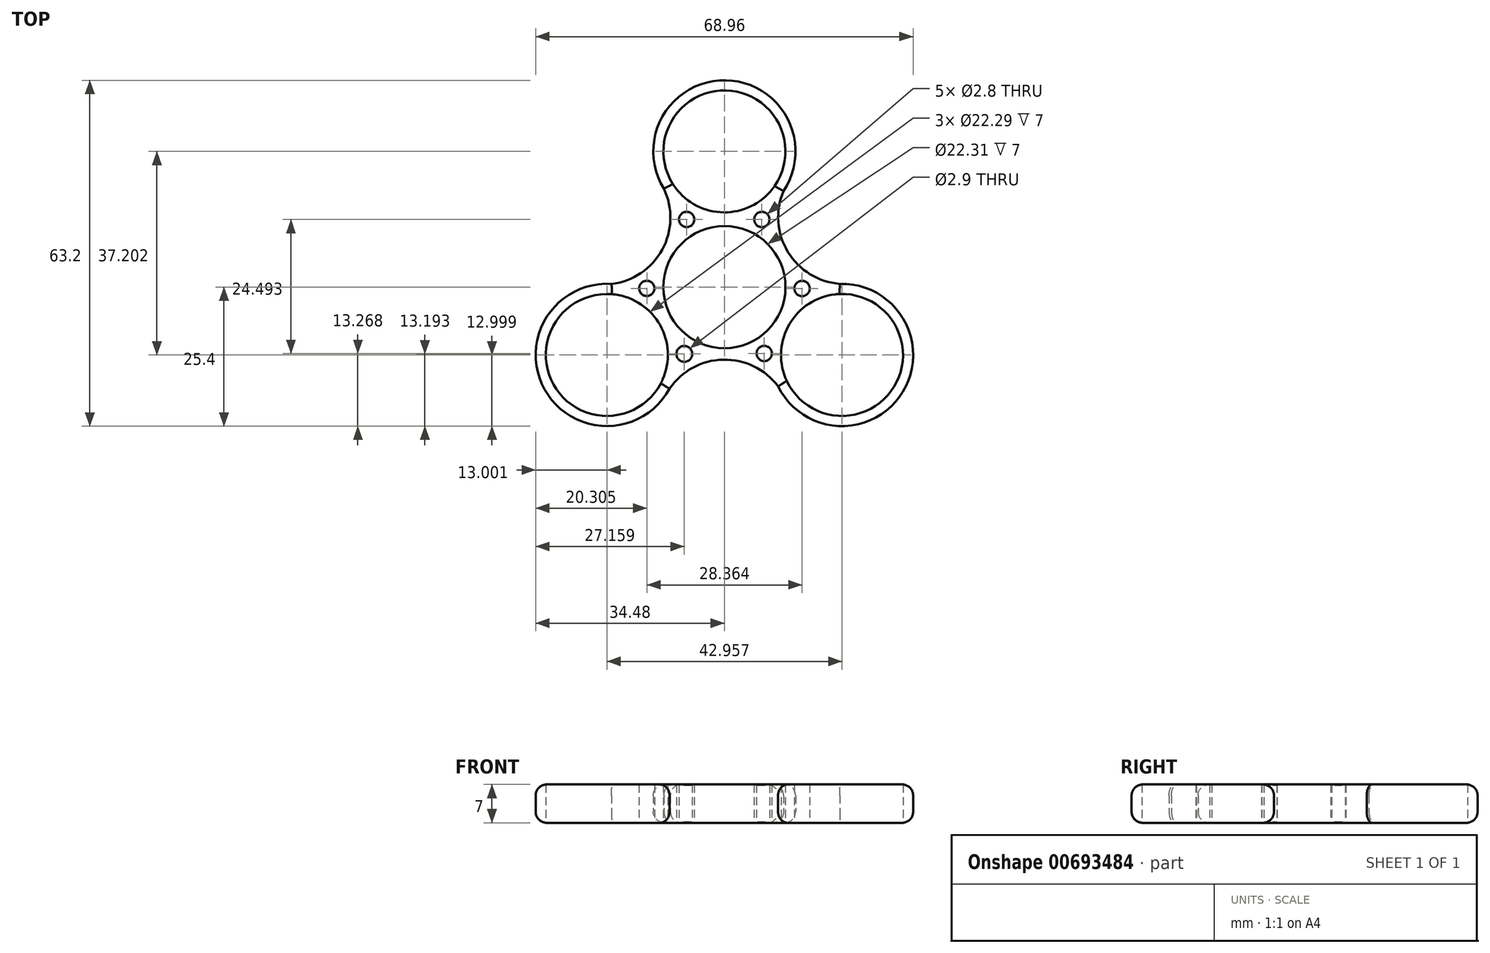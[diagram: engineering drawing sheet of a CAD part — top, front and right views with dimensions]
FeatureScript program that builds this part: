
annotation { "Feature Type Name" : "Feature", "Feature Type Description" : "" }
export const myFeature = defineFeature(function(context is Context, id is Id, definition is map)
    precondition{}
    {
        {
            var Q0;
            Q0=qCreatedBy(makeId("Top.planeOp"),FACE);
            var sketch = newSketch(context, id + "F0", { "sketchPlane" : qUnion([Q0])});
            skCircle(sketch, "E0", {"center": v(0, 0) * mm, "radius": 11.15 * mm});
            skCircle(sketch, "E1", {"center": v(0, 0) * mm, "radius": 13 * mm});
            skCircle(sketch, "E2", {"center": v(0, 24.8) * mm, "radius": 11.14 * mm});
            skCircle(sketch, "E3", {"center": v(0, 24.8) * mm, "radius": 13 * mm});
            skCircle(sketch, "E4.1.0", {"center": v(-21.48, -12.4) * mm, "radius": 13 * mm});
            skCircle(sketch, "E4.1.1", {"center": v(-21.48, -12.4) * mm, "radius": 11.14 * mm});
            skCircle(sketch, "E4.2.0", {"center": v(21.48, -12.4) * mm, "radius": 13 * mm});
            skCircle(sketch, "E4.2.1", {"center": v(21.48, -12.4) * mm, "radius": 11.14 * mm});
            skArc(sketch, "E5", {"start": v(-20.6, 0.57) * mm, "mid": v(-11.37, 6.82) * mm, "end": v(-11.06, 17.97) * mm});
            skArc(sketch, "E6.1.0", {"start": v(9.8, -18.12) * mm, "mid": v(-0.22, -13.26) * mm, "end": v(-10.03, -18.56) * mm});
            skArc(sketch, "E6.2.0", {"start": v(10.8, 17.56) * mm, "mid": v(11.6, 6.44) * mm, "end": v(21.09, 0.6) * mm});
            skSolve(sketch);
        }
        {
            var Q0;
            {var subQ0=sQuery(id+"F0.wireOp",EDGE,"E3");var subQ1=sQuery(id+"F0.wireOp",EDGE,"E1");var subQ2=makeQuery(id+"F0.imprint","INTERSECT",VERTEX,{"disambiguationData":[OD(0.0)],"derivedFrom":[subQ1,subQ0]});Q0=makeQuery(id+"F0.imprint","IMPRINT",FACE,{"disambiguationData":[TD([[makeQuery(id+"F0.imprint","IMPRINT",EDGE,{"disambiguationData":[TD([[subQ2,1.0]])],"derivedFrom":subQ1}),1.0]])]});}
            var Q1;
            Q1=makeQuery(id+"F0.imprint","IMPRINT",FACE,{"disambiguationData":[TD([[makeQuery(id+"F0.imprint","IMPRINT",EDGE,{"derivedFrom":sQuery(id+"F0.wireOp",EDGE,"E2")}),-1.0]])]});
            var Q2;
            Q2=makeQuery(id+"F0.imprint","IMPRINT",FACE,{"disambiguationData":[TD([[makeQuery(id+"F0.imprint","IMPRINT",EDGE,{"derivedFrom":sQuery(id+"F0.wireOp",EDGE,"E4.2.1")}),-1.0]])]});
            var Q3;
            Q3=makeQuery(id+"F0.imprint","IMPRINT",FACE,{"disambiguationData":[TD([[makeQuery(id+"F0.imprint","IMPRINT",EDGE,{"derivedFrom":sQuery(id+"F0.wireOp",EDGE,"E4.1.1")}),-1.0]])]});
            var Q4;
            {var subQ0=sQuery(id+"F0.wireOp",EDGE,"E4.1.0");var subQ1=sQuery(id+"F0.wireOp",EDGE,"E1");var subQ2=makeQuery(id+"F0.imprint","INTERSECT",VERTEX,{"disambiguationData":[OD(0.0)],"derivedFrom":[subQ1,subQ0]});Q4=makeQuery(id+"F0.imprint","IMPRINT",FACE,{"disambiguationData":[TD([[makeQuery(id+"F0.imprint","IMPRINT",EDGE,{"disambiguationData":[TD([[subQ2,-1.0]])],"derivedFrom":subQ1}),1.0]])]});}
            var Q5;
            {var subQ0=sQuery(id+"F0.wireOp",EDGE,"E4.2.0");var subQ1=sQuery(id+"F0.wireOp",EDGE,"E1");var subQ2=makeQuery(id+"F0.imprint","INTERSECT",VERTEX,{"disambiguationData":[OD(0.0)],"derivedFrom":[subQ1,subQ0]});Q5=makeQuery(id+"F0.imprint","IMPRINT",FACE,{"disambiguationData":[TD([[makeQuery(id+"F0.imprint","IMPRINT",EDGE,{"disambiguationData":[TD([[subQ2,-1.0]])],"derivedFrom":subQ1}),1.0]])]});}
            var Q6;
            Q6=makeQuery(id+"F0.imprint","IMPRINT",FACE,{"disambiguationData":[TD([[makeQuery(id+"F0.imprint","IMPRINT",EDGE,{"derivedFrom":sQuery(id+"F0.wireOp",EDGE,"E0")}),-1.0]])]});
            var Q7;
            {var subQ5=sQuery(id+"F0.wireOp",EDGE,"E6.2.0");Q7=makeQuery(id+"F0.imprint","IMPRINT",FACE,{"disambiguationData":[TD([[makeQuery(id+"F0.imprint","IMPRINT",EDGE,{"derivedFrom":subQ5}),-1.0]])]});}
            var Q8;
            {var subQ5=sQuery(id+"F0.wireOp",EDGE,"E5");Q8=makeQuery(id+"F0.imprint","IMPRINT",FACE,{"disambiguationData":[TD([[makeQuery(id+"F0.imprint","IMPRINT",EDGE,{"derivedFrom":subQ5}),-1.0]])]});}
            var Q9;
            {var subQ5=sQuery(id+"F0.wireOp",EDGE,"E6.1.0");Q9=makeQuery(id+"F0.imprint","IMPRINT",FACE,{"disambiguationData":[TD([[makeQuery(id+"F0.imprint","IMPRINT",EDGE,{"derivedFrom":subQ5}),-1.0]])]});}
            extrude(context, id + "F1", {"entities" : qUnion([Q0, Q1, Q2, Q3, Q4, Q5, Q6, Q7, Q8, Q9]), "depth" : 7 * mm, "offsetDistance" : 25 * mm});
        }
        {
            var Q0;
            Q0=makeQuery(id+"F1.opExtrude","CAP_EDGE",EDGE,{"disambiguationData":[OSD([sQuery(id+"F0.wireOp",EDGE,"E5")])],"isStart":false});
            var Q1;
            Q1=makeQuery(id+"F1.opExtrude","CAP_EDGE",EDGE,{"disambiguationData":[OSD([sQuery(id+"F0.wireOp",EDGE,"E6.1.0")])],"isStart":false});
            var Q2;
            Q2=makeQuery(id+"F1.opExtrude","CAP_EDGE",EDGE,{"disambiguationData":[OSD([sQuery(id+"F0.wireOp",EDGE,"E6.2.0")])],"isStart":false});
            var Q3;
            Q3=makeQuery(id+"F1.opExtrude","CAP_EDGE",EDGE,{"disambiguationData":[OSD([sQuery(id+"F0.wireOp",EDGE,"E5")])],"isStart":true});
            var Q4;
            Q4=makeQuery(id+"F1.opExtrude","CAP_EDGE",EDGE,{"disambiguationData":[OSD([sQuery(id+"F0.wireOp",EDGE,"E6.1.0")])],"isStart":true});
            var Q5;
            Q5=makeQuery(id+"F1.opExtrude","CAP_EDGE",EDGE,{"disambiguationData":[OSD([sQuery(id+"F0.wireOp",EDGE,"E6.2.0")])],"isStart":true});
            fillet(context, id + "F2", {"entities" : qUnion([Q0, Q1, Q2, Q3, Q4, Q5]), "radius" : 2 * mm, "tangentPropagation" : true, "allowEdgeOverflow" : false});
        }
        {
            var Q0;
            Q0=makeQuery(id+"F1.opExtrude","CAP_EDGE",EDGE,{"disambiguationData":[OSD([sQuery(id+"F0.wireOp",EDGE,"E4.2.0")])],"isStart":false});
            var Q1;
            Q1=makeQuery(id+"F1.opExtrude","CAP_EDGE",EDGE,{"disambiguationData":[OSD([sQuery(id+"F0.wireOp",EDGE,"E3")])],"isStart":false});
            var Q2;
            Q2=makeQuery(id+"F1.opExtrude","CAP_EDGE",EDGE,{"disambiguationData":[OSD([sQuery(id+"F0.wireOp",EDGE,"E4.1.0")])],"isStart":false});
            var Q3;
            Q3=makeQuery(id+"F1.opExtrude","CAP_EDGE",EDGE,{"disambiguationData":[OSD([sQuery(id+"F0.wireOp",EDGE,"E4.1.0")])],"isStart":true});
            var Q4;
            Q4=makeQuery(id+"F1.opExtrude","CAP_EDGE",EDGE,{"disambiguationData":[OSD([sQuery(id+"F0.wireOp",EDGE,"E4.2.0")])],"isStart":true});
            var Q5;
            Q5=makeQuery(id+"F1.opExtrude","CAP_EDGE",EDGE,{"disambiguationData":[OSD([sQuery(id+"F0.wireOp",EDGE,"E3")])],"isStart":true});
            fillet(context, id + "F3", {"entities" : qUnion([Q0, Q1, Q2, Q3, Q4, Q5]), "radius" : 2 * mm, "tangentPropagation" : true, "allowEdgeOverflow" : false});
        }
        {
            var Q0;
            Q0=qCreatedBy(makeId("Top.planeOp"),FACE);
            var sketch = newSketch(context, id + "F4", { "sketchPlane" : qUnion([Q0])});
            skCircle(sketch, "E7", {"center": v(-6.9, 12.36) * mm, "radius": 1.4 * mm});
            skCircle(sketch, "E8", {"center": v(6.84, 12.36) * mm, "radius": 1.4 * mm});
            skCircle(sketch, "E9", {"center": v(7.28, -12.13) * mm, "radius": 1.4 * mm});
            skCircle(sketch, "E10", {"center": v(-7.32, -12.2) * mm, "radius": 1.45 * mm});
            skCircle(sketch, "E11", {"center": v(14.19, -0.26) * mm, "radius": 1.4 * mm});
            skCircle(sketch, "E12", {"center": v(-14.18, -0.23) * mm, "radius": 1.4 * mm});
            skSolve(sketch);
        }
        {
            var Q0;
            Q0=makeQuery(id+"F4.imprint","IMPRINT",FACE,{"disambiguationData":[TD([[makeQuery(id+"F4.imprint","IMPRINT",EDGE,{"derivedFrom":sQuery(id+"F4.wireOp",EDGE,"E10")}),1.0]])]});
            var Q1;
            Q1=makeQuery(id+"F4.imprint","IMPRINT",FACE,{"disambiguationData":[TD([[makeQuery(id+"F4.imprint","IMPRINT",EDGE,{"derivedFrom":sQuery(id+"F4.wireOp",EDGE,"E9")}),1.0]])]});
            var Q2;
            Q2=makeQuery(id+"F4.imprint","IMPRINT",FACE,{"disambiguationData":[TD([[makeQuery(id+"F4.imprint","IMPRINT",EDGE,{"derivedFrom":sQuery(id+"F4.wireOp",EDGE,"E11")}),1.0]])]});
            var Q3;
            Q3=makeQuery(id+"F4.imprint","IMPRINT",FACE,{"disambiguationData":[TD([[makeQuery(id+"F4.imprint","IMPRINT",EDGE,{"derivedFrom":sQuery(id+"F4.wireOp",EDGE,"E8")}),1.0]])]});
            var Q4;
            Q4=makeQuery(id+"F4.imprint","IMPRINT",FACE,{"disambiguationData":[TD([[makeQuery(id+"F4.imprint","IMPRINT",EDGE,{"derivedFrom":sQuery(id+"F4.wireOp",EDGE,"E12")}),1.0]])]});
            var Q5;
            Q5=makeQuery(id+"F4.imprint","IMPRINT",FACE,{"disambiguationData":[TD([[makeQuery(id+"F4.imprint","IMPRINT",EDGE,{"derivedFrom":sQuery(id+"F4.wireOp",EDGE,"E7")}),1.0]])]});
            extrude(context, id + "F5", {"entities" : qUnion([Q0, Q1, Q2, Q3, Q4, Q5]), "operationType" : NewBodyOperationType.REMOVE, "depth" : 7 * mm, "offsetDistance" : 25 * mm});
        }
    });
